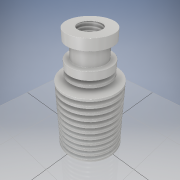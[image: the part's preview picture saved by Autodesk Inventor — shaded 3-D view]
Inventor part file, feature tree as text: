
AUTODESK INVENTOR PART (.ipt)
format: ipt  version: 2019 (Build 230136000, 136)  size: 614,400 bytes
history: native  units: mm
features: other x4, sketch x4, extrude x3, chamfer x1, fillet x1
ambient origin geometry x8: Origin, YZ Plane, XZ Plane, XY Plane, X Axis, Y Axis, Z Axis, Center Point
bodies: Solide1 (feature_tree)
feature tree (13):
  other  "Révolution1"
  extrude  "Extrusion1"  Depth=8.0mm
  extrude  "Extrusion2"  Depth=3.7mm
  extrude  "Extrusion3"  Depth=6.0mm
  chamfer  "Chanfrein1"  Distance=6.0mm
  other  "Filetage1"
  other  "Filetage2"
  fillet  "Congé1"  Radius=3.0mm
  sketch  "Esquisse1"
  other  "Image1"
  sketch  "Esquisse2"
  sketch  "Esquisse3"
  sketch  "Esquisse4"
